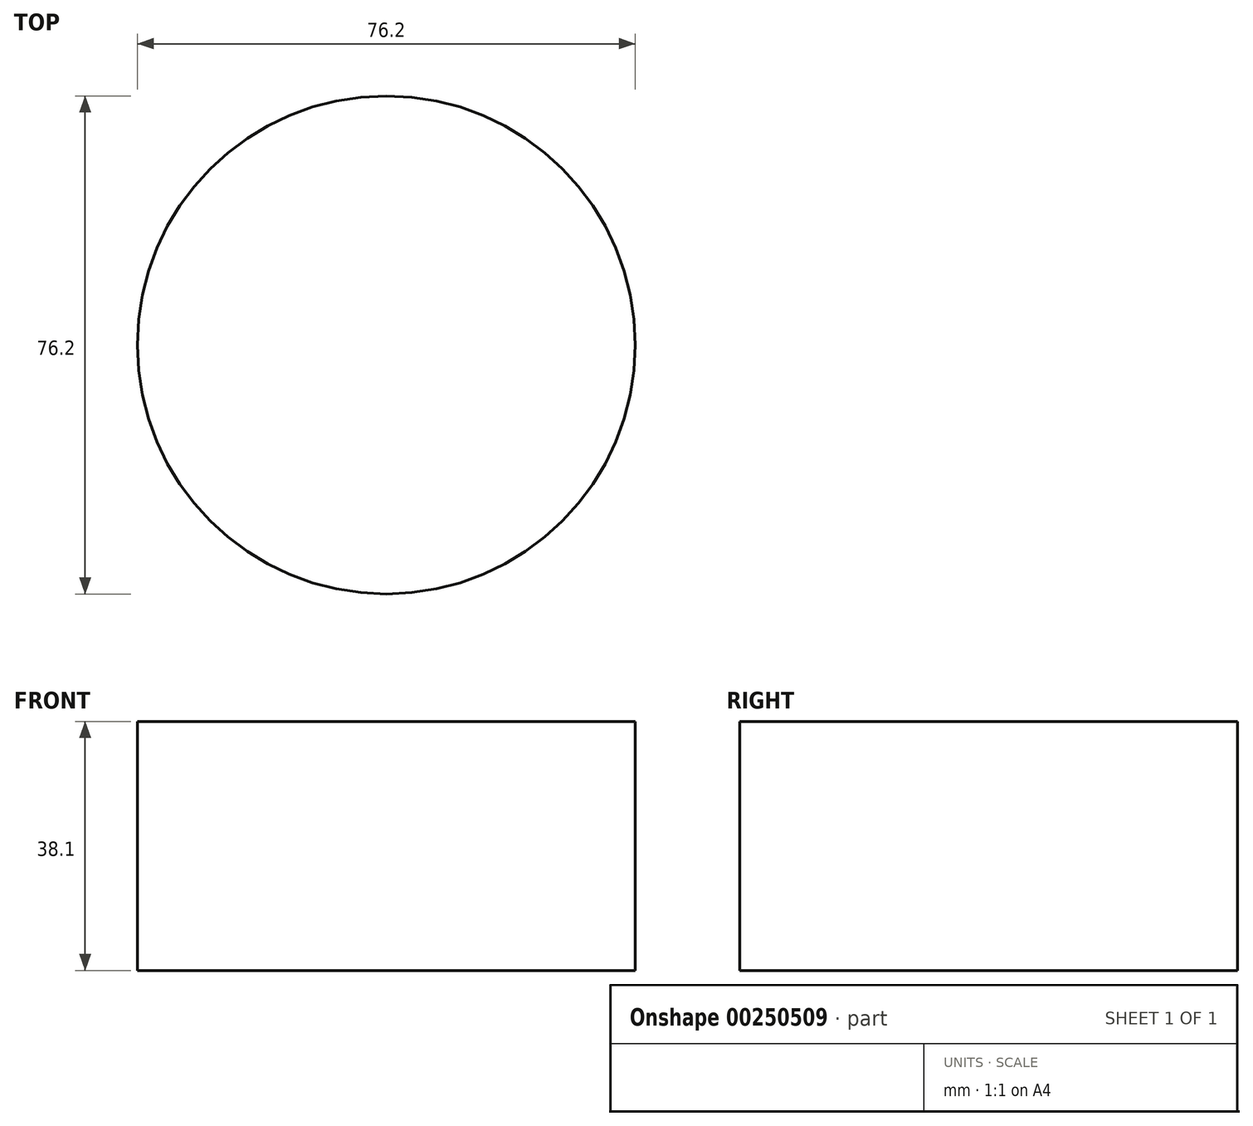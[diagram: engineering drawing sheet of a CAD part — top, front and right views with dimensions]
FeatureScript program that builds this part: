
annotation { "Feature Type Name" : "Feature", "Feature Type Description" : "" }
export const myFeature = defineFeature(function(context is Context, id is Id, definition is map)
    precondition{}
    {
        {
            var Q0;
            Q0=qCreatedBy(makeId("Top.planeOp"),FACE);
            var sketch = newSketch(context, id + "F0", { "sketchPlane" : qUnion([Q0])});
            skCircle(sketch, "E0", {"center": v(0, 0) * mm, "radius": 38.1 * mm});
            skSolve(sketch);
        }
        {
            var Q0;
            Q0=makeQuery(id+"F0.imprint","IMPRINT",FACE,{"disambiguationData":[TD([[makeQuery(id+"F0.imprint","IMPRINT",EDGE,{"derivedFrom":sQuery(id+"F0.wireOp",EDGE,"E0")}),1.0]])]});
            extrude(context, id + "F1", {"entities" : qUnion([Q0]), "oppositeDirection" : true, "depth" : 38.1 * mm});
        }
    });
